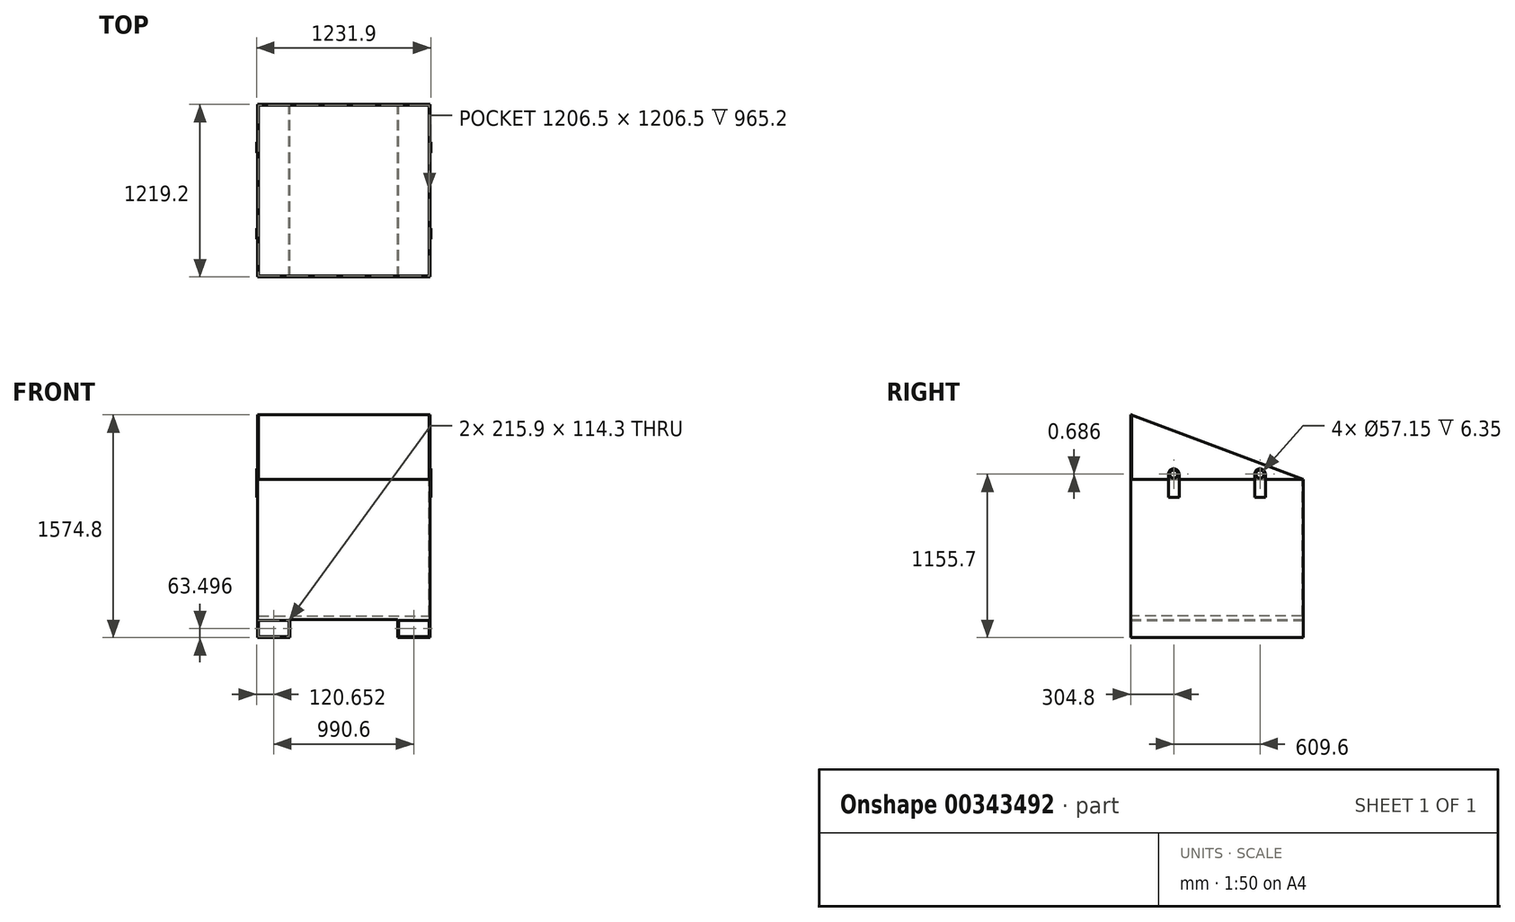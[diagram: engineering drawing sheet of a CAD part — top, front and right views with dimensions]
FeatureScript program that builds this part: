
annotation { "Feature Type Name" : "Feature", "Feature Type Description" : "" }
export const myFeature = defineFeature(function(context is Context, id is Id, definition is map)
    precondition{}
    {
        {
            var Q0;
            Q0=qCreatedBy(makeId("Front.planeOp"),FACE);
            var sketch = newSketch(context, id + "F0", { "sketchPlane" : qUnion([Q0])});
            skLineSegment(sketch, "E0", {"start": v(80.14, 1047.57) * mm, "end": v(80.14, 56.97) * mm});
            skLineSegment(sketch, "E1", {"start": v(80.14, 1047.57) * mm, "end": v(1299.34, 1047.57) * mm});
            skLineSegment(sketch, "E2", {"start": v(80.14, 56.97) * mm, "end": v(1299.34, 56.97) * mm});
            skLineSegment(sketch, "E3", {"start": v(1299.34, 56.97) * mm, "end": v(1299.34, 1047.57) * mm});
            skLineSegment(sketch, "E4", {"start": v(80.14, 56.97) * mm, "end": v(80.14, -70.03) * mm});
            skLineSegment(sketch, "E5", {"start": v(80.14, -70.03) * mm, "end": v(308.74, -70.03) * mm});
            skLineSegment(sketch, "E6", {"start": v(308.74, -70.03) * mm, "end": v(308.74, 56.97) * mm});
            skLineSegment(sketch, "E7.bottom", {"start": v(1299.34, 56.97) * mm, "end": v(1070.74, 56.97) * mm});
            skLineSegment(sketch, "E7.top", {"start": v(1299.34, -70.03) * mm, "end": v(1070.74, -70.03) * mm});
            skLineSegment(sketch, "E7.left", {"start": v(1299.34, 56.97) * mm, "end": v(1299.34, -70.03) * mm});
            skLineSegment(sketch, "E7.right", {"start": v(1070.74, 56.97) * mm, "end": v(1070.74, -70.03) * mm});
            skLineSegment(sketch, "E8.bottom", {"start": v(1293, 50.62) * mm, "end": v(1077.1, 50.62) * mm});
            skLineSegment(sketch, "E8.top", {"start": v(1293, -63.68) * mm, "end": v(1077.1, -63.68) * mm});
            skLineSegment(sketch, "E8.left", {"start": v(1293, 50.62) * mm, "end": v(1293, -63.68) * mm});
            skLineSegment(sketch, "E8.right", {"start": v(1077.1, 50.62) * mm, "end": v(1077.1, -63.68) * mm});
            skLineSegment(sketch, "E9.bottom", {"start": v(302.4, 50.62) * mm, "end": v(86.5, 50.62) * mm});
            skLineSegment(sketch, "E9.top", {"start": v(302.4, -63.68) * mm, "end": v(86.5, -63.68) * mm});
            skLineSegment(sketch, "E9.left", {"start": v(302.4, 50.62) * mm, "end": v(302.4, -63.68) * mm});
            skLineSegment(sketch, "E9.right", {"start": v(86.5, 50.62) * mm, "end": v(86.5, -63.68) * mm});
            skSolve(sketch);
        }
        {
            var Q0;
            Q0 = qSketchRegion(id + "F0", true);
            extrude(context, id + "F1", {"entities" : qUnion([Q0]), "depth" : 1219.2 * mm});
        }
        {
            var Q0;
            Q0=makeQuery(id+"F1.opExtrude","SWEPT_FACE",FACE,{"disambiguationData":[OSD([sQuery(id+"F0.wireOp",EDGE,"E1")])]});
            var sketch = newSketch(context, id + "F2", { "sketchPlane" : qUnion([Q0])});
            skLineSegment(sketch, "E10.bottom", {"start": v(86.5, -6.35) * mm, "end": v(1293, -6.35) * mm});
            skLineSegment(sketch, "E10.top", {"start": v(86.5, -1212.85) * mm, "end": v(1293, -1212.85) * mm});
            skLineSegment(sketch, "E10.left", {"start": v(86.5, -6.35) * mm, "end": v(86.5, -1212.85) * mm});
            skLineSegment(sketch, "E10.right", {"start": v(1293, -6.35) * mm, "end": v(1293, -1212.85) * mm});
            skSolve(sketch);
        }
        {
            var Q0;
            Q0 = qSketchRegion(id + "F2", true);
            extrude(context, id + "F3", {"entities" : qUnion([Q0]), "operationType" : NewBodyOperationType.REMOVE, "oppositeDirection" : true, "depth" : 965.2 * mm});
        }
        {
            var Q0;
            Q0=makeQuery(id+"F0.imprint","IMPRINT",FACE,{"disambiguationData":[TD([[makeQuery(id+"F0.imprint","IMPRINT",EDGE,{"derivedFrom":sQuery(id+"F0.wireOp",EDGE,"E8.bottom")}),1.0]])]});
            var Q1;
            Q1=makeQuery(id+"F0.imprint","IMPRINT",FACE,{"disambiguationData":[TD([[makeQuery(id+"F0.imprint","IMPRINT",EDGE,{"derivedFrom":sQuery(id+"F0.wireOp",EDGE,"E9.bottom")}),1.0]])]});
            extrude(context, id + "F4", {"entities" : qUnion([Q0, Q1]), "operationType" : NewBodyOperationType.REMOVE, "depth" : 1219.2 * mm});
        }
        {
            var Q0;
            Q0=makeQuery(id+"F1.opExtrude","SWEPT_FACE",FACE,{"disambiguationData":[OSD([sQuery(id+"F0.wireOp",EDGE,"E0"),sQuery(id+"F0.wireOp",EDGE,"E4")])]});
            var sketch = newSketch(context, id + "F5", { "sketchPlane" : qUnion([Q0])});
            skLineSegment(sketch, "E11.bottom", {"start": v(342.9, 921.25) * mm, "end": v(266.7, 921.25) * mm});
            skLineSegment(sketch, "E11.left", {"start": v(342.9, 921.25) * mm, "end": v(342.9, 1048.25) * mm});
            skLineSegment(sketch, "E11.right", {"start": v(266.7, 921.25) * mm, "end": v(266.7, 1048.25) * mm});
            skPoint(sketch, "E11.middle", {"position": v(304.8, 984.75) * mm});
            skLineSegment(sketch, "E12.bottom", {"start": v(952.5, 921.25) * mm, "end": v(876.3, 921.25) * mm});
            skLineSegment(sketch, "E12.left", {"start": v(952.5, 921.25) * mm, "end": v(952.5, 1048.25) * mm});
            skLineSegment(sketch, "E12.right", {"start": v(876.3, 921.25) * mm, "end": v(876.3, 1048.25) * mm});
            skPoint(sketch, "E12.middle", {"position": v(914.4, 984.75) * mm});
            skLineSegment(sketch, "E13.bottom", {"start": v(266.7, 1048.25) * mm, "end": v(342.9, 1048.25) * mm});
            skLineSegment(sketch, "E13.left", {"start": v(266.7, 1048.25) * mm, "end": v(266.7, 1086.35) * mm});
            skLineSegment(sketch, "E13.right", {"start": v(342.9, 1048.25) * mm, "end": v(342.9, 1086.35) * mm});
            skLineSegment(sketch, "E14.bottom", {"start": v(876.3, 1048.25) * mm, "end": v(952.5, 1048.25) * mm});
            skLineSegment(sketch, "E14.left", {"start": v(876.3, 1048.25) * mm, "end": v(876.3, 1086.35) * mm});
            skLineSegment(sketch, "E14.right", {"start": v(952.5, 1048.25) * mm, "end": v(952.5, 1086.35) * mm});
            skArc(sketch, "E15", {"start": v(342.9, 1086.35) * mm, "mid": v(304.8, 1124.45) * mm, "end": v(266.7, 1086.35) * mm});
            skArc(sketch, "E16", {"start": v(952.5, 1086.35) * mm, "mid": v(914.4, 1124.45) * mm, "end": v(876.3, 1086.35) * mm});
            skCircle(sketch, "E17", {"center": v(304.8, 1086.35) * mm, "radius": 28.58 * mm});
            skCircle(sketch, "E18", {"center": v(914.4, 1086.35) * mm, "radius": 28.58 * mm});
            skLineSegment(sketch, "E19", {"start": v(1219.2, 1047.57) * mm, "end": v(1219.2, 1504.77) * mm});
            skLineSegment(sketch, "E20", {"start": v(1219.2, 1504.77) * mm, "end": v(0, 1047.57) * mm});
            skSolve(sketch);
        }
        {
            var Q0;
            Q0=makeQuery(id+"F1.opExtrude","SWEPT_FACE",FACE,{"disambiguationData":[OSD([sQuery(id+"F0.wireOp",EDGE,"E3"),sQuery(id+"F0.wireOp",EDGE,"E7.left")])]});
            var sketch = newSketch(context, id + "F6", { "sketchPlane" : qUnion([Q0])});
            skLineSegment(sketch, "E21.bottom", {"start": v(-876.3, 920.57) * mm, "end": v(-952.5, 920.57) * mm});
            skLineSegment(sketch, "E21.top", {"start": v(-876.3, 1047.57) * mm, "end": v(-952.5, 1047.57) * mm});
            skLineSegment(sketch, "E21.left", {"start": v(-876.3, 920.57) * mm, "end": v(-876.3, 1047.57) * mm});
            skLineSegment(sketch, "E21.right", {"start": v(-952.5, 920.57) * mm, "end": v(-952.5, 1047.57) * mm});
            skPoint(sketch, "E21.middle", {"position": v(-914.4, 984.07) * mm});
            skLineSegment(sketch, "E22.bottom", {"start": v(-266.7, 920.57) * mm, "end": v(-342.9, 920.57) * mm});
            skLineSegment(sketch, "E22.top", {"start": v(-266.7, 1047.57) * mm, "end": v(-342.9, 1047.57) * mm});
            skLineSegment(sketch, "E22.left", {"start": v(-266.7, 920.57) * mm, "end": v(-266.7, 1047.57) * mm});
            skLineSegment(sketch, "E22.right", {"start": v(-342.9, 920.57) * mm, "end": v(-342.9, 1047.57) * mm});
            skPoint(sketch, "E22.middle", {"position": v(-304.8, 984.07) * mm});
            skLineSegment(sketch, "E23", {"start": v(-952.5, 1047.57) * mm, "end": v(-952.5, 1085.67) * mm});
            skLineSegment(sketch, "E24", {"start": v(-876.3, 1047.57) * mm, "end": v(-876.3, 1085.67) * mm});
            skArc(sketch, "E25", {"start": v(-876.3, 1085.67) * mm, "mid": v(-914.4, 1123.77) * mm, "end": v(-952.5, 1085.67) * mm});
            skCircle(sketch, "E26", {"center": v(-914.4, 1085.67) * mm, "radius": 28.58 * mm});
            skLineSegment(sketch, "E27", {"start": v(-342.9, 1047.57) * mm, "end": v(-342.9, 1085.67) * mm});
            skLineSegment(sketch, "E28", {"start": v(-266.7, 1047.57) * mm, "end": v(-266.7, 1085.67) * mm});
            skArc(sketch, "E29", {"start": v(-266.7, 1085.67) * mm, "mid": v(-304.8, 1123.77) * mm, "end": v(-342.9, 1085.67) * mm});
            skCircle(sketch, "E30", {"center": v(-304.8, 1085.67) * mm, "radius": 28.58 * mm});
            skLineSegment(sketch, "E31", {"start": v(-1219.2, 1047.57) * mm, "end": v(-1219.2, 1504.77) * mm});
            skLineSegment(sketch, "E32", {"start": v(-1219.2, 1504.77) * mm, "end": v(0, 1047.57) * mm});
            skSolve(sketch);
        }
        {
            var Q0;
            Q0=makeQuery(id+"F5.imprint","IMPRINT",FACE,{"disambiguationData":[TD([[makeQuery(id+"F5.imprint","IMPRINT",EDGE,{"derivedFrom":sQuery(id+"F5.wireOp",EDGE,"E13.bottom")}),1.0]])]});
            var Q1;
            {var subQ0=sQuery(id+"F5.wireOp",EDGE,"E11.bottom");Q1=makeQuery(id+"F5.imprint","IMPRINT",FACE,{"disambiguationData":[TD([[makeQuery(id+"F5.imprint","IMPRINT",EDGE,{"derivedFrom":subQ0}),-1.0]])]});}
            var Q2;
            {var subQ0=sQuery(id+"F5.wireOp",EDGE,"E12.bottom");Q2=makeQuery(id+"F5.imprint","IMPRINT",FACE,{"disambiguationData":[TD([[makeQuery(id+"F5.imprint","IMPRINT",EDGE,{"derivedFrom":subQ0}),-1.0]])]});}
            var Q3;
            Q3=makeQuery(id+"F5.imprint","IMPRINT",FACE,{"disambiguationData":[TD([[makeQuery(id+"F5.imprint","IMPRINT",EDGE,{"derivedFrom":sQuery(id+"F5.wireOp",EDGE,"E14.bottom")}),1.0]])]});
            extrude(context, id + "F7", {"entities" : qUnion([Q0, Q1, Q2, Q3]), "operationType" : NewBodyOperationType.ADD, "depth" : 6.35 * mm});
        }
        {
            var Q0;
            Q0=makeQuery(id+"F6.imprint","IMPRINT",FACE,{"disambiguationData":[TD([[makeQuery(id+"F6.imprint","IMPRINT",EDGE,{"derivedFrom":sQuery(id+"F6.wireOp",EDGE,"E21.bottom")}),-1.0]])]});
            var Q1;
            Q1=makeQuery(id+"F6.imprint","IMPRINT",FACE,{"disambiguationData":[TD([[makeQuery(id+"F6.imprint","IMPRINT",EDGE,{"derivedFrom":sQuery(id+"F6.wireOp",EDGE,"E21.top")}),1.0]])]});
            var Q2;
            Q2=makeQuery(id+"F6.imprint","IMPRINT",FACE,{"disambiguationData":[TD([[makeQuery(id+"F6.imprint","IMPRINT",EDGE,{"derivedFrom":sQuery(id+"F6.wireOp",EDGE,"E22.bottom")}),-1.0]])]});
            var Q3;
            Q3=makeQuery(id+"F6.imprint","IMPRINT",FACE,{"disambiguationData":[TD([[makeQuery(id+"F6.imprint","IMPRINT",EDGE,{"derivedFrom":sQuery(id+"F6.wireOp",EDGE,"E22.top")}),1.0]])]});
            extrude(context, id + "F8", {"entities" : qUnion([Q0, Q1, Q2, Q3]), "operationType" : NewBodyOperationType.ADD, "depth" : 6.35 * mm});
        }
        {
            var Q0;
            {var subQ2=sQuery(id+"F5.wireOp",EDGE,"E13.left");Q0=makeQuery(id+"F5.imprint","IMPRINT",FACE,{"disambiguationData":[TD([[makeQuery(id+"F5.imprint","IMPRINT",EDGE,{"derivedFrom":subQ2}),1.0]])]});}
            extrude(context, id + "F9", {"entities" : qUnion([Q0]), "oppositeDirection" : true, "depth" : 6.35 * mm});
        }
        {
            var Q0;
            {var subQ4=sQuery(id+"F6.wireOp",EDGE,"E23");Q0=makeQuery(id+"F6.imprint","IMPRINT",FACE,{"disambiguationData":[TD([[makeQuery(id+"F6.imprint","IMPRINT",EDGE,{"derivedFrom":subQ4}),1.0]])]});}
            extrude(context, id + "F10", {"entities" : qUnion([Q0]), "oppositeDirection" : true, "depth" : 6.35 * mm});
        }
        {
            var Q0;
            Q0=makeQuery(id+"F1.opExtrude","CAP_FACE",FACE,{"disambiguationData":[OSD([sQuery(id+"F0.wireOp",EDGE,"E0"),sQuery(id+"F0.wireOp",EDGE,"E1"),sQuery(id+"F0.wireOp",EDGE,"E2"),sQuery(id+"F0.wireOp",EDGE,"E3"),sQuery(id+"F0.wireOp",EDGE,"E4"),sQuery(id+"F0.wireOp",EDGE,"E5"),sQuery(id+"F0.wireOp",EDGE,"E6"),sQuery(id+"F0.wireOp",EDGE,"E7.top"),sQuery(id+"F0.wireOp",EDGE,"E7.left"),sQuery(id+"F0.wireOp",EDGE,"E7.right"),sQuery(id+"F0.wireOp",EDGE,"E8.bottom"),sQuery(id+"F0.wireOp",EDGE,"E8.top"),sQuery(id+"F0.wireOp",EDGE,"E8.left"),sQuery(id+"F0.wireOp",EDGE,"E8.right"),sQuery(id+"F0.wireOp",EDGE,"E9.bottom"),sQuery(id+"F0.wireOp",EDGE,"E9.top"),sQuery(id+"F0.wireOp",EDGE,"E9.left"),sQuery(id+"F0.wireOp",EDGE,"E9.right")])],"isStart":false});
            var sketch = newSketch(context, id + "F11", { "sketchPlane" : qUnion([Q0])});
            skLineSegment(sketch, "E33", {"start": v(80.14, 1047.57) * mm, "end": v(80.14, 1504.77) * mm});
            skLineSegment(sketch, "E34", {"start": v(80.14, 1504.77) * mm, "end": v(1299.34, 1504.77) * mm});
            skLineSegment(sketch, "E35", {"start": v(1299.34, 1504.77) * mm, "end": v(1299.34, 1047.57) * mm});
            skLineSegment(sketch, "E36", {"start": v(1299.34, 1047.57) * mm, "end": v(80.14, 1047.57) * mm});
            skSolve(sketch);
        }
        {
            var Q0;
            Q0=makeQuery(id+"F11.imprint","IMPRINT",FACE,{"disambiguationData":[TD([[makeQuery(id+"F11.imprint","IMPRINT",EDGE,{"derivedFrom":sQuery(id+"F11.wireOp",EDGE,"E33")}),-1.0]])]});
            extrude(context, id + "F12", {"entities" : qUnion([Q0]), "oppositeDirection" : true, "depth" : 6.35 * mm});
        }
    });
